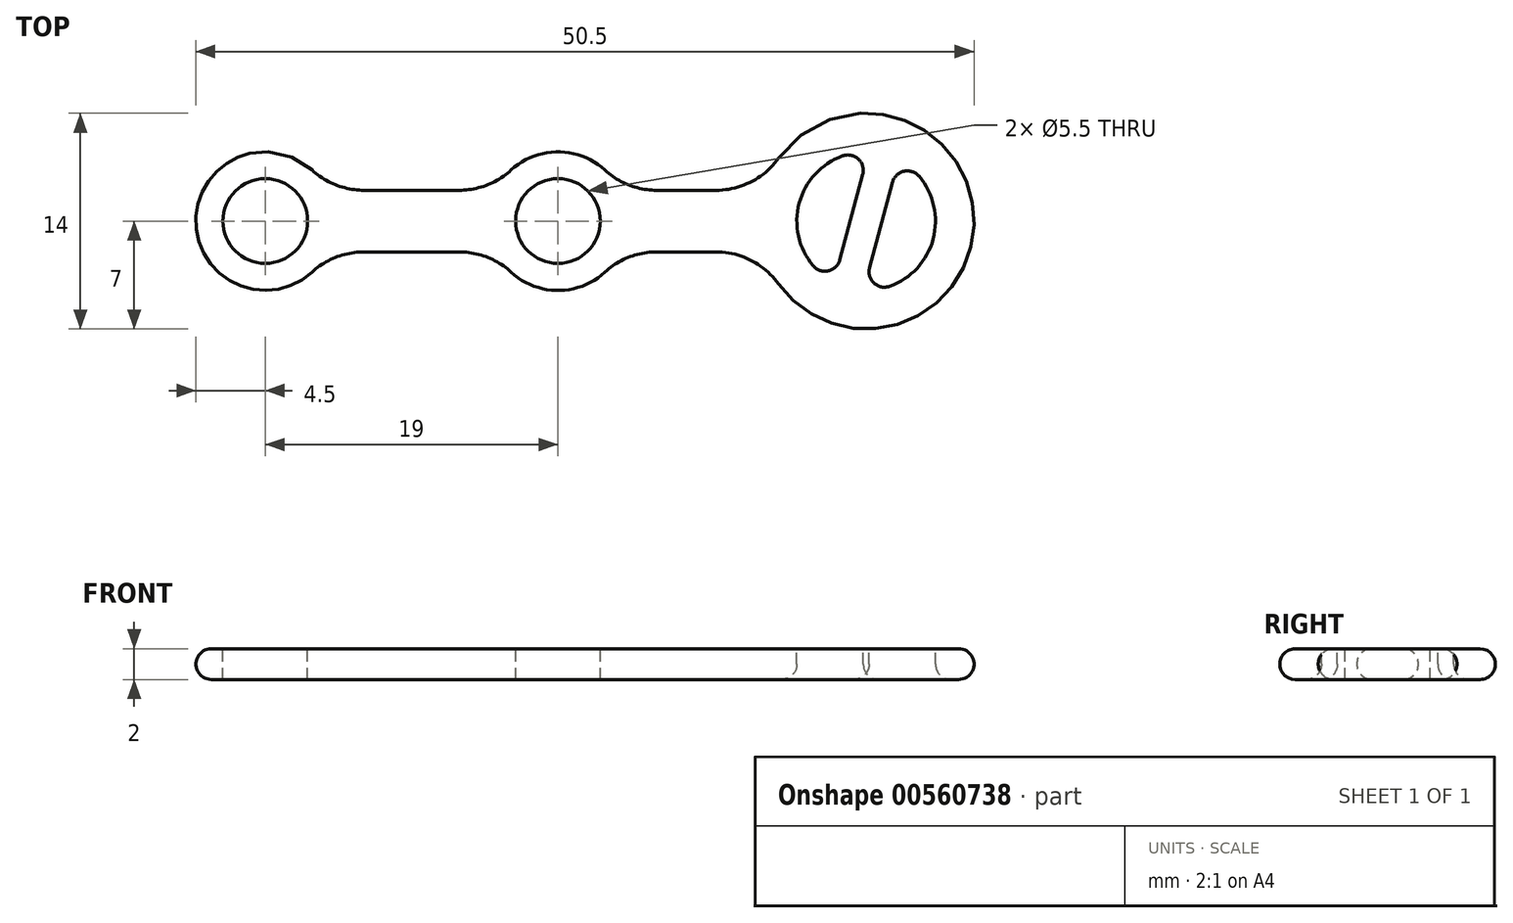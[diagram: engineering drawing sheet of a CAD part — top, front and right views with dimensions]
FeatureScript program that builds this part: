
annotation { "Feature Type Name" : "Feature", "Feature Type Description" : "" }
export const myFeature = defineFeature(function(context is Context, id is Id, definition is map)
    precondition{}
    {
        {
            var Q0;
            Q0=qCreatedBy(makeId("Top.planeOp"),FACE);
            var sketch = newSketch(context, id + "F0", { "sketchPlane" : qUnion([Q0])});
            skCircle(sketch, "E0", {"center": v(0, 0) * mm, "radius": 4.5 * mm});
            skCircle(sketch, "E1", {"center": v(-19, 0) * mm, "radius": 4.5 * mm});
            skCircle(sketch, "E2", {"center": v(20, 0) * mm, "radius": 7 * mm});
            skLineSegment(sketch, "E3", {"start": v(-14.97, 2) * mm, "end": v(-4.03, 2) * mm});
            skLineSegment(sketch, "E4", {"start": v(4.03, 2) * mm, "end": v(13.3, 2) * mm});
            skLineSegment(sketch, "E5.MirrorCS", {"start": v(-14.97, -2) * mm, "end": v(-4.03, -2) * mm});
            skLineSegment(sketch, "E6.MirrorCS", {"start": v(4.03, -2) * mm, "end": v(13.3, -2) * mm});
            skSolve(sketch);
        }
        {
            var Q0;
            Q0 = qSketchRegion(id + "F0", true);
            extrude(context, id + "F1", {"entities" : qUnion([Q0]), "depth" : 2 * mm, "offsetDistance" : 25 * mm});
        }
        {
            var Q0;
            Q0=makeQuery(id+"F1.opExtrude","CAP_FACE",FACE,{"disambiguationData":[OSD([sQuery(id+"F0.wireOp",EDGE,"E0"),sQuery(id+"F0.wireOp",EDGE,"E1"),sQuery(id+"F0.wireOp",EDGE,"E2"),sQuery(id+"F0.wireOp",EDGE,"E3"),sQuery(id+"F0.wireOp",EDGE,"E4"),sQuery(id+"F0.wireOp",EDGE,"E5.MirrorCS"),sQuery(id+"F0.wireOp",EDGE,"E6.MirrorCS")])],"isStart":false});
            var sketch = newSketch(context, id + "F2", { "sketchPlane" : qUnion([Q0])});
            skCircle(sketch, "E7", {"center": v(-19, 0) * mm, "radius": 2.75 * mm});
            skCircle(sketch, "E8", {"center": v(0, 0) * mm, "radius": 2.75 * mm});
            skArc(sketch, "E9", {"start": v(19.83, -4.5) * mm, "mid": v(24.35, -1.16) * mm, "end": v(22.1, 3.98) * mm});
            skLineSegment(sketch, "E10", {"start": v(20.17, 4.5) * mm, "end": v(17.9, -3.98) * mm});
            skLineSegment(sketch, "E11", {"start": v(22.1, 3.98) * mm, "end": v(19.83, -4.5) * mm});
            skLineSegment(sketch, "E12", {"start": v(19.03, 0.26) * mm, "end": v(20, 0) * mm, "construction": true});
            skLineSegment(sketch, "E13", {"start": v(20.97, -0.26) * mm, "end": v(20, 0) * mm, "construction": true});
            skArc(sketch, "E14.trimOffspring", {"start": v(20.17, 4.5) * mm, "mid": v(15.65, 1.16) * mm, "end": v(17.9, -3.98) * mm});
            skSolve(sketch);
        }
        {
            var Q0;
            Q0 = qSketchRegion(id + "F2", true);
            extrude(context, id + "F3", {"entities" : qUnion([Q0]), "operationType" : NewBodyOperationType.REMOVE, "endBound" : BoundingType.THROUGH_ALL, "oppositeDirection" : true, "depth" : 25 * mm, "offsetDistance" : 25 * mm});
        }
        {
            var Q0;
            {var subQ0=sQuery(id+"F2.wireOp",EDGE,"E11");var subQ1=sQuery(id+"F2.wireOp",EDGE,"E9");Q0=makeQuery(id+"F3.boolean.opBoolean","COPY",EDGE,{"derivedFrom":makeQuery(id+"F3.opExtrude","SWEPT_EDGE",EDGE,{"disambiguationData":[OSD([subQ1,subQ0]),TDD([makeQuery(id+"F2.imprint","INTERSECT",VERTEX,{"disambiguationData":[OD(1.0)],"derivedFrom":[subQ1,subQ0]})])]})});}
            var Q1;
            {var subQ0=sQuery(id+"F2.wireOp",EDGE,"E14.trimOffspring");var subQ1=sQuery(id+"F2.wireOp",EDGE,"E10");Q1=makeQuery(id+"F3.boolean.opBoolean","COPY",EDGE,{"derivedFrom":makeQuery(id+"F3.opExtrude","SWEPT_EDGE",EDGE,{"disambiguationData":[OSD([subQ1,subQ0]),TDD([makeQuery(id+"F2.imprint","INTERSECT",VERTEX,{"disambiguationData":[OD(1.0)],"derivedFrom":[subQ1,subQ0]})])]})});}
            var Q2;
            {var subQ0=sQuery(id+"F2.wireOp",EDGE,"E11");var subQ1=sQuery(id+"F2.wireOp",EDGE,"E9");Q2=makeQuery(id+"F3.boolean.opBoolean","COPY",EDGE,{"derivedFrom":makeQuery(id+"F3.opExtrude","SWEPT_EDGE",EDGE,{"disambiguationData":[OSD([subQ1,subQ0]),TDD([makeQuery(id+"F2.imprint","INTERSECT",VERTEX,{"disambiguationData":[OD(0.0)],"derivedFrom":[subQ1,subQ0]})])]})});}
            var Q3;
            {var subQ0=sQuery(id+"F2.wireOp",EDGE,"E14.trimOffspring");var subQ1=sQuery(id+"F2.wireOp",EDGE,"E10");Q3=makeQuery(id+"F3.boolean.opBoolean","COPY",EDGE,{"derivedFrom":makeQuery(id+"F3.opExtrude","SWEPT_EDGE",EDGE,{"disambiguationData":[OSD([subQ1,subQ0]),TDD([makeQuery(id+"F2.imprint","INTERSECT",VERTEX,{"disambiguationData":[OD(0.0)],"derivedFrom":[subQ1,subQ0]})])]})});}
            fillet(context, id + "F4", {"entities" : qUnion([Q0, Q1, Q2, Q3]), "radius" : 1 * mm, "tangentPropagation" : true, "allowEdgeOverflow" : false});
        }
        {
            var Q0;
            Q0=makeQuery(id+"F1.opExtrude","SWEPT_EDGE",EDGE,{"disambiguationData":[OSD([sQuery(id+"F0.wireOp",EDGE,"E1"),sQuery(id+"F0.wireOp",EDGE,"E3")])]});
            var Q1;
            Q1=makeQuery(id+"F1.opExtrude","SWEPT_EDGE",EDGE,{"disambiguationData":[OSD([sQuery(id+"F0.wireOp",EDGE,"E0"),sQuery(id+"F0.wireOp",EDGE,"E3")])]});
            var Q2;
            Q2=makeQuery(id+"F1.opExtrude","SWEPT_EDGE",EDGE,{"disambiguationData":[OSD([sQuery(id+"F0.wireOp",EDGE,"E0"),sQuery(id+"F0.wireOp",EDGE,"E4")])]});
            var Q3;
            Q3=makeQuery(id+"F1.opExtrude","SWEPT_EDGE",EDGE,{"disambiguationData":[OSD([sQuery(id+"F0.wireOp",EDGE,"E2"),sQuery(id+"F0.wireOp",EDGE,"E4")])]});
            var Q4;
            Q4=makeQuery(id+"F1.opExtrude","SWEPT_EDGE",EDGE,{"disambiguationData":[OSD([sQuery(id+"F0.wireOp",EDGE,"E1"),sQuery(id+"F0.wireOp",EDGE,"E5.MirrorCS")])]});
            var Q5;
            Q5=makeQuery(id+"F1.opExtrude","SWEPT_EDGE",EDGE,{"disambiguationData":[OSD([sQuery(id+"F0.wireOp",EDGE,"E0"),sQuery(id+"F0.wireOp",EDGE,"E5.MirrorCS")])]});
            var Q6;
            Q6=makeQuery(id+"F1.opExtrude","SWEPT_EDGE",EDGE,{"disambiguationData":[OSD([sQuery(id+"F0.wireOp",EDGE,"E0"),sQuery(id+"F0.wireOp",EDGE,"E6.MirrorCS")])]});
            var Q7;
            Q7=makeQuery(id+"F1.opExtrude","SWEPT_EDGE",EDGE,{"disambiguationData":[OSD([sQuery(id+"F0.wireOp",EDGE,"E2"),sQuery(id+"F0.wireOp",EDGE,"E6.MirrorCS")])]});
            fillet(context, id + "F5", {"entities" : qUnion([Q0, Q1, Q2, Q3, Q4, Q5, Q6, Q7]), "radius" : 5 * mm, "tangentPropagation" : true, "allowEdgeOverflow" : false});
        }
        {
            var Q0;
            {var subQ0=sQuery(id+"F0.wireOp",EDGE,"E5.MirrorCS");var subQ1=sQuery(id+"F0.wireOp",EDGE,"E1");Q0=makeQuery(id+"F5.opFillet","BLEND_EDGE",EDGE,{"blendedFrom":[makeQuery(id+"F1.opExtrude","SWEPT_EDGE",EDGE,{"disambiguationData":[OSD([subQ1,subQ0])]}),makeQuery(id+"F1.opExtrude","CAP_FACE",FACE,{"disambiguationData":[OSD([sQuery(id+"F0.wireOp",EDGE,"E0"),subQ1,sQuery(id+"F0.wireOp",EDGE,"E2"),sQuery(id+"F0.wireOp",EDGE,"E3"),sQuery(id+"F0.wireOp",EDGE,"E4"),subQ0,sQuery(id+"F0.wireOp",EDGE,"E6.MirrorCS")])],"isStart":false})],"blendedInto":[makeQuery(id+"F1.opExtrude","CAP_FACE",FACE,{"disambiguationData":[OSD([sQuery(id+"F0.wireOp",EDGE,"E0"),subQ1,sQuery(id+"F0.wireOp",EDGE,"E2"),sQuery(id+"F0.wireOp",EDGE,"E3"),sQuery(id+"F0.wireOp",EDGE,"E4"),subQ0,sQuery(id+"F0.wireOp",EDGE,"E6.MirrorCS")])],"isStart":false})]});}
            var Q1;
            Q1=makeQuery(id+"F3.boolean.opBoolean","COPY",EDGE,{"derivedFrom":makeQuery(id+"F3.opExtrude","CAP_EDGE",EDGE,{"disambiguationData":[OSD([sQuery(id+"F2.wireOp",EDGE,"E14.trimOffspring")])],"isStart":true})});
            var Q2;
            Q2=makeQuery(id+"F3.boolean.opBoolean","COPY",EDGE,{"derivedFrom":makeQuery(id+"F3.opExtrude","CAP_EDGE",EDGE,{"disambiguationData":[OSD([sQuery(id+"F2.wireOp",EDGE,"E11")])],"isStart":true})});
            var Q3;
            Q3=makeQuery(id+"F1.opExtrude","CAP_EDGE",EDGE,{"disambiguationData":[OSD([sQuery(id+"F0.wireOp",EDGE,"E3")])],"isStart":true});
            var Q4;
            Q4=makeQuery(id+"F3.boolean.opBoolean","INTERSECT",EDGE,{"derivedFrom":[makeQuery(id+"F1.opExtrude","CAP_FACE",FACE,{"disambiguationData":[OSD([sQuery(id+"F0.wireOp",EDGE,"E0"),sQuery(id+"F0.wireOp",EDGE,"E1"),sQuery(id+"F0.wireOp",EDGE,"E2"),sQuery(id+"F0.wireOp",EDGE,"E3"),sQuery(id+"F0.wireOp",EDGE,"E4"),sQuery(id+"F0.wireOp",EDGE,"E5.MirrorCS"),sQuery(id+"F0.wireOp",EDGE,"E6.MirrorCS")])],"isStart":true}),makeQuery(id+"F3.opExtrude","SWEPT_FACE",FACE,{"disambiguationData":[OSD([sQuery(id+"F2.wireOp",EDGE,"E10")])]})]});
            var Q5;
            Q5=makeQuery(id+"F3.boolean.opBoolean","INTERSECT",EDGE,{"derivedFrom":[makeQuery(id+"F1.opExtrude","CAP_FACE",FACE,{"disambiguationData":[OSD([sQuery(id+"F0.wireOp",EDGE,"E0"),sQuery(id+"F0.wireOp",EDGE,"E1"),sQuery(id+"F0.wireOp",EDGE,"E2"),sQuery(id+"F0.wireOp",EDGE,"E3"),sQuery(id+"F0.wireOp",EDGE,"E4"),sQuery(id+"F0.wireOp",EDGE,"E5.MirrorCS"),sQuery(id+"F0.wireOp",EDGE,"E6.MirrorCS")])],"isStart":true}),makeQuery(id+"F3.opExtrude","SWEPT_FACE",FACE,{"disambiguationData":[OSD([sQuery(id+"F2.wireOp",EDGE,"E11")])]})]});
            fillet(context, id + "F6", {"entities" : qUnion([Q0, Q1, Q2, Q3, Q4, Q5]), "radius" : 1 * mm, "tangentPropagation" : true, "allowEdgeOverflow" : false});
        }
    });
